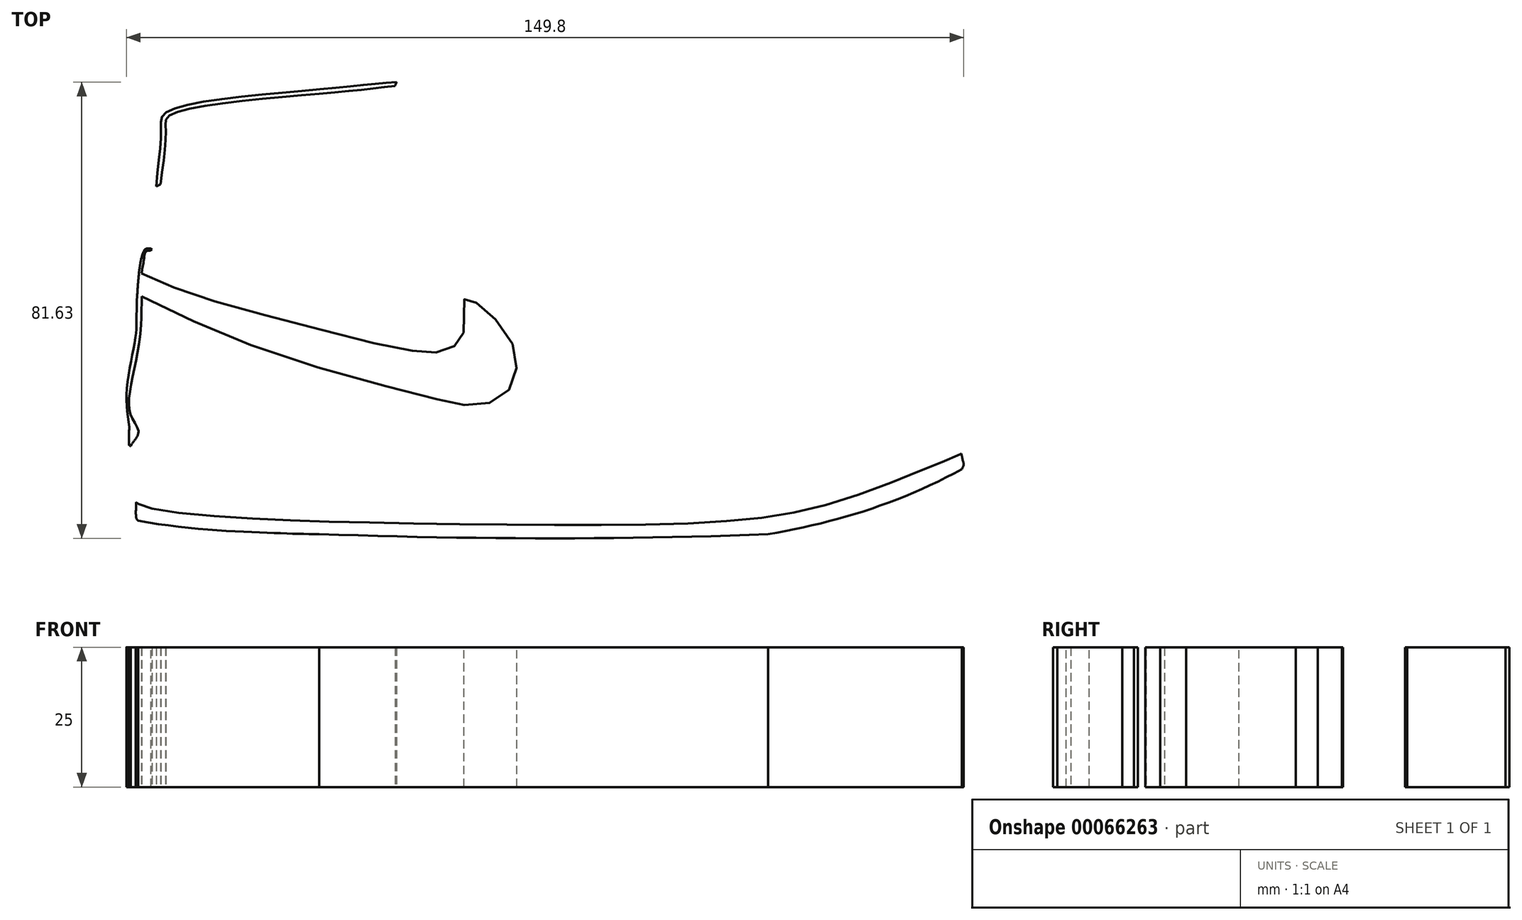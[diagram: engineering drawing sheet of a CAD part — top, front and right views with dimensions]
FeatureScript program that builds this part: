
annotation { "Feature Type Name" : "Feature", "Feature Type Description" : "" }
export const myFeature = defineFeature(function(context is Context, id is Id, definition is map)
    precondition{}
    {
        {
            var Q0;
            Q0=qCreatedBy(makeId("Top.planeOp"),FACE);
            var sketch = newSketch(context, id + "F0", { "sketchPlane" : qUnion([Q0])});
            skFitSpline(sketch, "E0", {"points": [v(-76.49, 41.77) * mm, v(-75.31, 28.32) * mm, v(-74.9, 25.02) * mm], "startDerivative": vector(-1.79, -23.98) * mm, "endDerivative": vector(5.53, -3) * mm});
            skFitSpline(sketch, "E1", {"points": [v(-74.9, 25.02) * mm, v(-51.7, 22.86) * mm, v(-42.5, 22.6) * mm], "startDerivative": vector(41.41, -7.73) * mm, "endDerivative": vector(21.02, 0) * mm});
            skFitSpline(sketch, "E2", {"points": [v(-42.5, 22.6) * mm, v(37.83, 22.6) * mm], "startDerivative": vector(79.88, -2.73) * mm, "endDerivative": vector(77.93, 3.24) * mm});
            skFitSpline(sketch, "E3", {"points": [v(37.83, 22.6) * mm, v(72.45, 34.26) * mm], "startDerivative": vector(35.9, 6.1) * mm, "endDerivative": vector(31.98, 17.98) * mm});
            skFitSpline(sketch, "E4", {"points": [v(72.45, 34.26) * mm, v(72.55, 36.35) * mm], "startDerivative": vector(1.87, 2.61) * mm, "endDerivative": vector(-0.4, 3.16) * mm});
            skFitSpline(sketch, "E5", {"points": [v(2.77, 69.25) * mm, v(-9.68, 77.21) * mm, v(-16.74, 79) * mm, v(-16.38, 84.72) * mm, v(-15.63, 91.22) * mm, v(-18.7, 101.5) * mm, v(-21.94, 103.5) * mm], "startDerivative": vector(-36.15, 21.9) * mm, "endDerivative": vector(-39.69, 6.6) * mm});
            skFitSpline(sketch, "E6", {"points": [v(-21.94, 103.5) * mm, v(-28.67, 103.5) * mm, v(-44.35, 102.04) * mm, v(-70.03, 98.02) * mm, v(-70.81, 94.89) * mm, v(-71.85, 82.1) * mm, v(-72.64, 73.75) * mm, v(-73.62, 73.63) * mm, v(-75.18, 62.72) * mm, v(-75.37, 57.85) * mm, v(-76.93, 48.7) * mm, v(-76.49, 41.77) * mm], "startDerivative": vector(-70.55, 3.02) * mm, "endDerivative": vector(12, -77.48) * mm});
            skFitSpline(sketch, "E7", {"points": [v(-75.31, 28.32) * mm, v(-73.39, 27.4) * mm, v(-57.28, 25.57) * mm, v(-32.2, 24.65) * mm, v(3.07, 24.24) * mm, v(32.11, 25.07) * mm, v(49.8, 28.32) * mm, v(66.17, 34.4) * mm, v(72.76, 37.17) * mm], "startDerivative": vector(31.59, -21.22) * mm, "endDerivative": vector(76.46, 33.83) * mm});
            skFitSpline(sketch, "E8", {"points": [v(-76.49, 41.77) * mm, v(-71.58, 40.11) * mm, v(-43.76, 38.15) * mm, v(21.75, 34.88) * mm, v(35.58, 35.02) * mm, v(57.13, 38.55) * mm, v(69.43, 42.66) * mm], "startDerivative": vector(48.6, -22.52) * mm, "endDerivative": vector(90.4, 33.96) * mm});
            skFitSpline(sketch, "E9", {"points": [v(-74.74, 69.45) * mm, v(-65.65, 65.7) * mm, v(-47.02, 60.43) * mm, v(-27.93, 55.77) * mm, v(-22.67, 55.17) * mm, v(-19.52, 55.47) * mm, v(-17.56, 56.97) * mm, v(-16.66, 58.63) * mm, v(-16.36, 65.24) * mm, v(-15, 64.49) * mm, v(-11.7, 61.78) * mm, v(-7.95, 56.67) * mm, v(-7.2, 52.47) * mm, v(-8.4, 48.7) * mm, v(-11.4, 46.3) * mm, v(-16.06, 45.7) * mm, v(-21.32, 46.76) * mm, v(-50.32, 54.87) * mm, v(-75.07, 65.53) * mm], "startDerivative": vector(128.25, -58.68) * mm, "endDerivative": vector(-210.1, 103.25) * mm});
            skFitSpline(sketch, "E10", {"points": [v(3.05, 35.8) * mm, v(5.4, 41.4) * mm, v(7.66, 48.9) * mm, v(7.48, 53.95) * mm, v(2.28, 56.57) * mm, v(-3.67, 60.92) * mm, v(-7.55, 65.53) * mm, v(-12.65, 68.05) * mm, v(-18.69, 69.25) * mm, v(-20.93, 69.25) * mm, v(-24.74, 71.45) * mm, v(-25.5, 74.99) * mm, v(-25.45, 78.71) * mm, v(-25.37, 79) * mm, v(-25.38, 83.03) * mm, v(-27.6, 81.67) * mm, v(-34.73, 78.18) * mm, v(-40.13, 75.75) * mm, v(-43.26, 73.31) * mm, v(-45.35, 69.25) * mm, v(-46.4, 67.22) * mm, v(-54.22, 67.74) * mm, v(-69.71, 71.75) * mm, v(-72.64, 73.75) * mm], "startDerivative": vector(47.55, 118.02) * mm, "endDerivative": vector(-57.37, 54.49) * mm});
            skFitSpline(sketch, "E11", {"points": [v(-71.67, 84.83) * mm, v(-54.2, 93.6) * mm, v(-41.86, 97.98) * mm, v(-29.73, 101.94) * mm, v(-28.67, 103.5) * mm], "startDerivative": vector(54.83, 28.85) * mm, "endDerivative": vector(7.75, 18) * mm});
            skFitSpline(sketch, "E12", {"points": [v(-62.6, 76.47) * mm, v(-61.26, 77.4) * mm, v(-60.2, 78.17) * mm, v(-59.09, 78.75) * mm, v(-58.5, 78.99) * mm, v(-58.09, 79.16) * mm, v(-58.5, 79.87) * mm, v(-59.15, 80.57) * mm, v(-59.62, 81.22) * mm, v(-59.97, 81.57) * mm, v(-59.2, 82.16) * mm, v(-58.09, 82.5) * mm, v(-57.27, 82.92) * mm, v(-56.33, 83.86) * mm, v(-55.92, 84.85) * mm, v(-55.4, 85.85) * mm, v(-54.8, 86.73) * mm, v(-53.92, 87.79) * mm, v(-52.99, 88.38) * mm, v(-51.4, 89.14) * mm, v(-50.17, 89.26) * mm, v(-48.53, 89.26) * mm, v(-46.83, 89.14) * mm, v(-45.71, 88.96) * mm, v(-44.89, 88.96) * mm, v(-44.13, 89.31) * mm, v(-43.19, 89.78) * mm, v(-42.48, 90.25) * mm, v(-42.25, 90.02) * mm, v(-41.78, 88.9) * mm, v(-41.2, 87.44) * mm, v(-40.6, 87.67) * mm, v(-38.02, 88.79) * mm, v(-35.62, 89.9) * mm, v(-35.52, 89.96) * mm, v(-35.6, 89.65) * mm, v(-36.5, 88.37) * mm, v(-37.48, 86.75) * mm, v(-38.63, 85.1) * mm, v(-40.18, 82.94) * mm, v(-41.31, 81.3) * mm, v(-43.19, 80.06) * mm, v(-45.95, 78.48) * mm, v(-48.66, 77.05) * mm, v(-50.1, 76.31) * mm, v(-52.76, 76.21) * mm, v(-55.57, 76.16) * mm, v(-57.94, 76.16) * mm, v(-60.1, 76.26) * mm, v(-62.6, 76.47) * mm]});
            skFitSpline(sketch, "E13", {"points": [v(-70.9, 85.24) * mm, v(-69.98, 95) * mm, v(-69.34, 97.5) * mm, v(-44.19, 101.26) * mm, v(-28.81, 102.85) * mm], "startDerivative": vector(6.58, 49.65) * mm, "endDerivative": vector(44.24, 5.31) * mm});
            skFitSpline(sketch, "E14", {"points": [v(-74.85, 41.07) * mm, v(-76.24, 43.88) * mm, v(-76.29, 48.66) * mm, v(-74.59, 57.85) * mm, v(-74.3, 62.72) * mm, v(-74.27, 65.14) * mm], "startDerivative": vector(-2.63, 15.24) * mm, "endDerivative": vector(0.4, 15.5) * mm});
            skFitSpline(sketch, "E15", {"points": [v(-74.33, 69.26) * mm, v(-73.94, 71.41) * mm, v(-73.48, 73.2) * mm, v(-72.95, 73.34) * mm, v(-72.4, 73.53) * mm], "startDerivative": vector(1.18, 5.99) * mm, "endDerivative": vector(3.1, 1.36) * mm});
            skFitSpline(sketch, "E16", {"points": [v(-74.85, 28) * mm, v(-76.38, 30.1) * mm, v(-76.22, 38.42) * mm, v(-74.85, 41.07) * mm], "startDerivative": vector(-1.28, 5.86) * mm, "endDerivative": vector(1.06, 14.55) * mm});
            skFitSpline(sketch, "E17", {"points": [v(7.48, 53.95) * mm, v(7.89, 56.17) * mm, v(7.48, 57.62) * mm, v(7.18, 59.69) * mm, v(7.22, 61.87) * mm, v(8.3, 63.8) * mm, v(9.46, 64.14) * mm, v(11.65, 64.21) * mm], "startDerivative": vector(4.4, 15.38) * mm, "endDerivative": vector(14.21, 2.03) * mm});
            skFitSpline(sketch, "E18", {"points": [v(71.14, 40.18) * mm, v(71.14, 40.62) * mm, v(70.84, 41.18) * mm, v(70.34, 41.93) * mm, v(69.89, 42.33) * mm, v(69.43, 42.66) * mm, v(69.25, 43.67) * mm, v(68.74, 46.07) * mm, v(67.6, 48.26) * mm, v(66.13, 50.35) * mm, v(63.83, 51.77) * mm, v(62.07, 52.18) * mm, v(55.34, 52.83) * mm, v(50.43, 53.21) * mm, v(46.16, 53.53) * mm, v(39.3, 54.65) * mm, v(31.5, 56.64) * mm, v(28.76, 57.5) * mm, v(28.76, 57.5) * mm, v(20.08, 60.7) * mm, v(16.34, 62.17) * mm, v(11.65, 64.21) * mm, v(11.65, 64.21) * mm, v(7.57, 66.08) * mm, v(2.77, 69.25) * mm], "startDerivative": vector(4.54, 27.8) * mm, "endDerivative": vector(-75.34, 54.46) * mm});
            skFitSpline(sketch, "E19", {"points": [v(28.76, 57.5) * mm, v(28.76, 56.14) * mm, v(29.58, 54.98) * mm, v(31.83, 53.57) * mm, v(32.82, 52.57) * mm, v(32.58, 51.24) * mm, v(31.91, 49.9) * mm, v(31.66, 49.58) * mm, v(32.08, 48.66) * mm, v(32.08, 47.58) * mm, v(31.33, 46.42) * mm, v(31.05, 45.85) * mm, v(30.57, 44.67) * mm, v(30.45, 44.03) * mm, v(30.7, 43.13) * mm, v(31.3, 42.4) * mm, v(32.18, 42.03) * mm, v(33.66, 42.01) * mm, v(34.76, 42.63) * mm, v(35.95, 43.94) * mm, v(36.8, 45) * mm, v(38.89, 46.76) * mm, v(44.09, 48.1) * mm, v(51.75, 49.19) * mm, v(61.25, 50.5) * mm, v(62.07, 50.83) * mm, v(62.65, 51.32) * mm, v(62.07, 52.18) * mm], "startDerivative": vector(-4.58, -41.3) * mm, "endDerivative": vector(-32.1, 31.17) * mm});
            skFitSpline(sketch, "E20", {"points": [v(21.75, 34.88) * mm, v(22.9, 37.33) * mm, v(25.48, 41.24) * mm, v(28.06, 44.7) * mm, v(31.66, 49.58) * mm], "startDerivative": vector(4.95, 11.68) * mm, "endDerivative": vector(12.79, 17.4) * mm});
            skFitSpline(sketch, "E21", {"points": [v(70.48, 39.85) * mm, v(71.14, 40.18) * mm], "startDerivative": vector(0.75, 0.3) * mm, "endDerivative": vector(0.75, 0.3) * mm});
            skFitSpline(sketch, "E22.trimOffspring", {"points": [v(-77.75, 39.05) * mm, v(-77.22, 38.8) * mm, v(-76.35, 38.42) * mm, v(-74.99, 37.92) * mm, v(-73.85, 37.57) * mm, v(-72.58, 37.25) * mm, v(-70.69, 36.88) * mm, v(-68, 36.52) * mm, v(-64.16, 36.17) * mm, v(-59.7, 35.9) * mm, v(-54.57, 35.64) * mm, v(-49.74, 35.42) * mm, v(-45.54, 35.23) * mm, v(-41.1, 35.03) * mm, v(-35.16, 34.75) * mm, v(-27.58, 34.37) * mm, v(-19.76, 33.97) * mm, v(-11.88, 33.56) * mm, v(-1.59, 33.03) * mm, v(8.01, 32.53) * mm, v(15.11, 32.18) * mm, v(18.7, 32.01) * mm, v(21.13, 31.9) * mm, v(23.27, 31.81) * mm, v(25.8, 31.72) * mm, v(28.51, 31.66) * mm, v(30.95, 31.7) * mm, v(32.92, 31.8) * mm, v(34.46, 31.9) * mm, v(36.1, 32.05) * mm, v(37.9, 32.24) * mm, v(39.82, 32.46) * mm, v(42.52, 32.81) * mm, v(46.07, 33.32) * mm, v(50.43, 34.05) * mm, v(54.66, 34.87) * mm, v(59.86, 36.08) * mm, v(64.02, 37.42) * mm, v(67.74, 38.8) * mm, v(69.55, 39.5) * mm, v(70.48, 39.85) * mm]});
            skFitSpline(sketch, "E23", {"points": [v(72.55, 36.35) * mm, v(72.44, 36.74) * mm, v(72.4, 37) * mm], "startDerivative": vector(-0.16, 0.76) * mm, "endDerivative": vector(-0.37, 0.53) * mm});
            skFitSpline(sketch, "E24", {"points": [v(71.14, 40.18) * mm, v(71.25, 39.85) * mm, v(71.46, 39.48) * mm, v(71.88, 39.13) * mm, v(72.4, 37) * mm], "startDerivative": vector(0.61, -1.87) * mm, "endDerivative": vector(0.85, -6.18) * mm});
            skFitSpline(sketch, "E25", {"points": [v(72.14, 36.9) * mm, v(71.99, 37.7) * mm, v(71.76, 38.8) * mm, v(71.36, 39.2) * mm, v(70.96, 39.73) * mm, v(70.89, 40.09) * mm], "startDerivative": vector(-0.72, 3.35) * mm, "endDerivative": vector(-0.2, 2.29) * mm});
            skFitSpline(sketch, "E26", {"points": [v(9.46, 64.14) * mm, v(16.35, 61.25) * mm, v(28.7, 56.8) * mm], "startDerivative": vector(14.83, -6.5) * mm, "endDerivative": vector(23.29, -8.1) * mm});
            skFitSpline(sketch, "E27", {"points": [v(62.65, 51.32) * mm, v(64.02, 50.76) * mm, v(65.5, 49.8) * mm, v(66.7, 48.12) * mm, v(67.75, 46.31) * mm, v(68.23, 44.35) * mm, v(68.44, 42.29) * mm], "startDerivative": vector(9.22, -3.52) * mm, "endDerivative": vector(0.98, -11.9) * mm});
            skSolve(sketch);
        }
        {
            var Q0;
            {var subQ0=sQuery(id+"F0.wireOp",EDGE,"E11");var subQ1=sQuery(id+"F0.wireOp",EDGE,"E6");var subQ2=makeQuery(id+"F0.imprint","INTERSECT",VERTEX,{"disambiguationData":[OD(0.0)],"derivedFrom":[subQ1,subQ0]});Q0=makeQuery(id+"F0.imprint","IMPRINT",FACE,{"disambiguationData":[TD([[makeQuery(id+"F0.imprint","IMPRINT",EDGE,{"disambiguationData":[TD([[subQ2,1.0]])],"derivedFrom":subQ1}),1.0]])]});}
            var Q1;
            {var subQ9=sQuery(id+"F0.wireOp",EDGE,"E5");Q1=makeQuery(id+"F0.imprint","IMPRINT",FACE,{"disambiguationData":[TD([[makeQuery(id+"F0.imprint","IMPRINT",EDGE,{"derivedFrom":subQ9}),1.0]])]});}
            var Q2;
            {var subQ5=sQuery(id+"F0.wireOp",EDGE,"E15");Q2=makeQuery(id+"F0.imprint","IMPRINT",FACE,{"disambiguationData":[TD([[makeQuery(id+"F0.imprint","IMPRINT",EDGE,{"derivedFrom":subQ5}),1.0]])]});}
            var Q3;
            {var subQ0=sQuery(id+"F0.wireOp",EDGE,"E9");var subQ1=sQuery(id+"F0.wireOp",EDGE,"E6");var subQ2=makeQuery(id+"F0.imprint","INTERSECT",VERTEX,{"disambiguationData":[OD(0.0)],"derivedFrom":[subQ1,subQ0]});Q3=makeQuery(id+"F0.imprint","IMPRINT",FACE,{"disambiguationData":[TD([[makeQuery(id+"F0.imprint","IMPRINT",EDGE,{"disambiguationData":[TD([[subQ2,-1.0]])],"derivedFrom":subQ1}),1.0]])]});}
            var Q4;
            {var subQ5=sQuery(id+"F0.wireOp",EDGE,"E14");Q4=makeQuery(id+"F0.imprint","IMPRINT",FACE,{"disambiguationData":[TD([[makeQuery(id+"F0.imprint","IMPRINT",EDGE,{"derivedFrom":subQ5}),1.0]])]});}
            var Q5;
            {var subQ4=sQuery(id+"F0.wireOp",EDGE,"E22.trimOffspring");Q5=makeQuery(id+"F0.imprint","IMPRINT",FACE,{"disambiguationData":[TD([[makeQuery(id+"F0.imprint","IMPRINT",EDGE,{"derivedFrom":subQ4}),1.0]])]});}
            var Q6;
            {var subQ4=sQuery(id+"F0.wireOp",EDGE,"E1");Q6=makeQuery(id+"F0.imprint","IMPRINT",FACE,{"disambiguationData":[TD([[makeQuery(id+"F0.imprint","IMPRINT",EDGE,{"derivedFrom":subQ4}),1.0]])]});}
            extrude(context, id + "F1", {"entities" : qUnion([Q0, Q1, Q2, Q3, Q4, Q5, Q6]), "depth" : 25 * mm});
        }
    });
